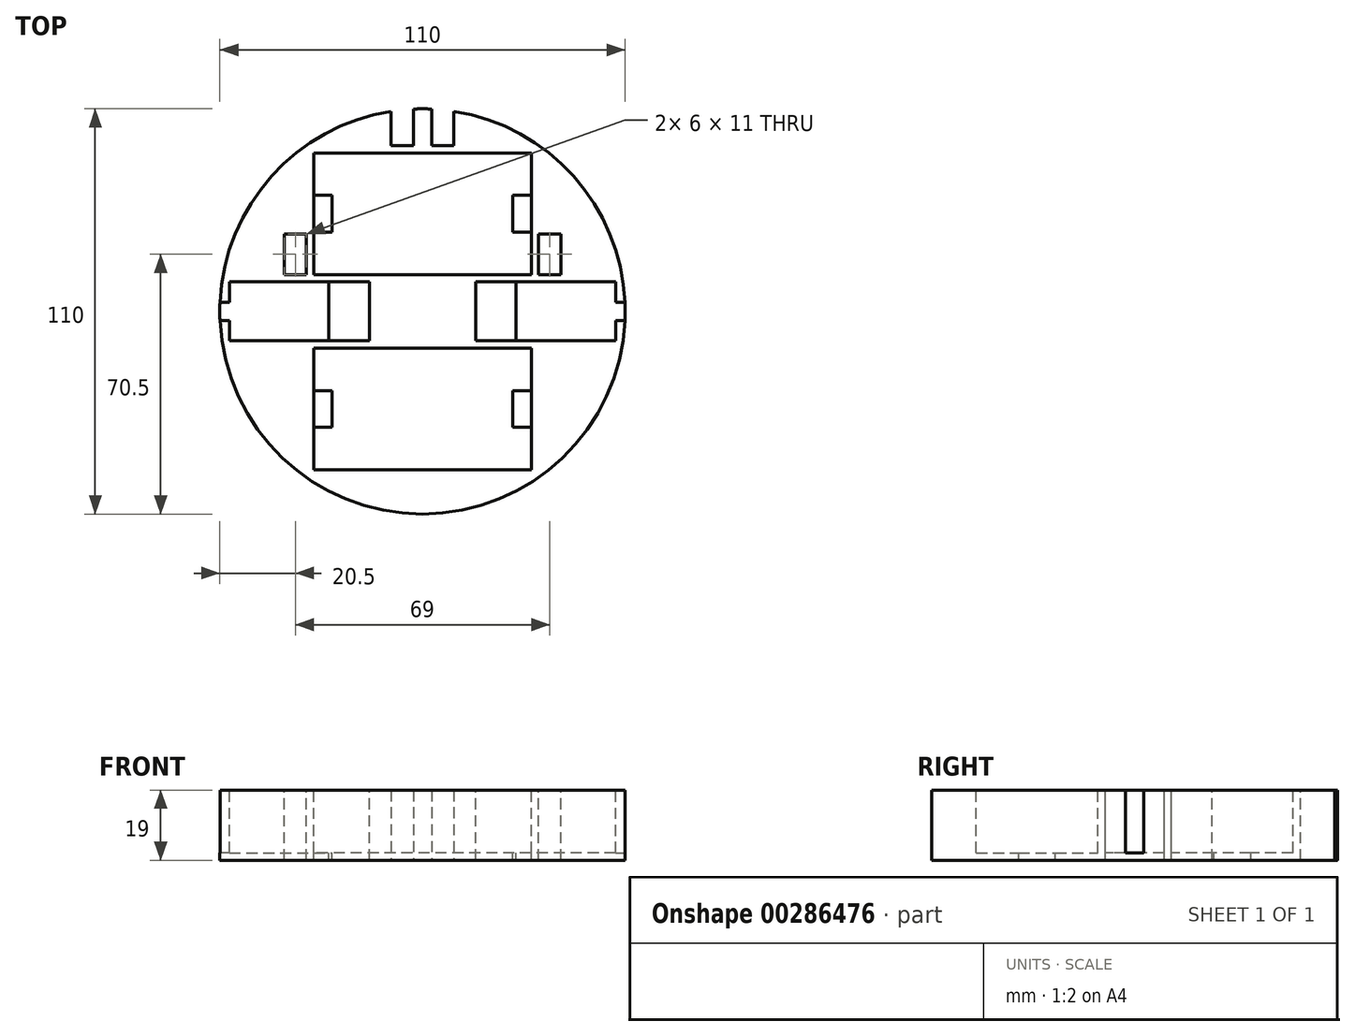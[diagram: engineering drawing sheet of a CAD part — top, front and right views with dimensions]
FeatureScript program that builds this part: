
annotation { "Feature Type Name" : "Feature", "Feature Type Description" : "" }
export const myFeature = defineFeature(function(context is Context, id is Id, definition is map)
    precondition{}
    {
        {
            var Q0;
            Q0=qCreatedBy(makeId("Top.planeOp"),FACE);
            var sketch = newSketch(context, id + "F0", { "sketchPlane" : qUnion([Q0])});
            skCircle(sketch, "E0", {"center": v(0, 0) * mm, "radius": 55 * mm});
            skSolve(sketch);
        }
        {
            var Q0;
            Q0=qSketchRegion(id+"F0",true);
            extrude(context, id + "F1", {"entities" : qUnion([Q0]), "depth" : 19 * mm, "offsetDistance" : 25 * mm});
        }
        {
            var Q0;
            Q0=makeQuery(id+"F1.opExtrude","CAP_FACE",FACE,{"disambiguationData":[OSD([sQuery(id+"F0.wireOp",EDGE,"E0")])],"isStart":false});
            var sketch = newSketch(context, id + "F2", { "sketchPlane" : qUnion([Q0])});
            skLineSegment(sketch, "E1.bottom", {"start": v(52.4, 8) * mm, "end": v(14.4, 8) * mm});
            skLineSegment(sketch, "E1.top", {"start": v(52.4, -8) * mm, "end": v(14.4, -8) * mm});
            skLineSegment(sketch, "E1.left", {"start": v(52.4, 8) * mm, "end": v(52.4, -8) * mm});
            skLineSegment(sketch, "E1.right", {"start": v(14.4, 8) * mm, "end": v(14.4, -8) * mm});
            skPoint(sketch, "E1.middle", {"position": v(33.4, 0) * mm});
            skLineSegment(sketch, "E2.bottom", {"start": v(52.4, 2.5) * mm, "end": v(57.6, 2.5) * mm});
            skLineSegment(sketch, "E2.top", {"start": v(52.4, -2.5) * mm, "end": v(57.6, -2.5) * mm});
            skLineSegment(sketch, "E2.left", {"start": v(52.4, 2.5) * mm, "end": v(52.4, -2.5) * mm});
            skLineSegment(sketch, "E2.right", {"start": v(57.6, 2.5) * mm, "end": v(57.6, -2.5) * mm});
            skPoint(sketch, "E2.middle", {"position": v(55, 0) * mm});
            skLineSegment(sketch, "E3.bottom", {"start": v(29.5, 43) * mm, "end": v(-29.5, 43) * mm});
            skLineSegment(sketch, "E3.top", {"start": v(29.5, 10) * mm, "end": v(-29.5, 10) * mm});
            skLineSegment(sketch, "E3.left", {"start": v(29.5, 43) * mm, "end": v(29.5, 10) * mm});
            skLineSegment(sketch, "E3.right", {"start": v(-29.5, 43) * mm, "end": v(-29.5, 10) * mm});
            skPoint(sketch, "E3.middle", {"position": v(0, 26.5) * mm});
            skLineSegment(sketch, "E4.MirrorCS", {"start": v(29.5, -10) * mm, "end": v(-29.5, -10) * mm});
            skLineSegment(sketch, "E5.MirrorCS", {"start": v(29.5, -43) * mm, "end": v(29.5, -10) * mm});
            skLineSegment(sketch, "E6.MirrorCS", {"start": v(29.5, -43) * mm, "end": v(-29.5, -43) * mm});
            skLineSegment(sketch, "E7.MirrorCS", {"start": v(-29.5, -43) * mm, "end": v(-29.5, -10) * mm});
            skLineSegment(sketch, "E8.MirrorCS", {"start": v(-52.4, 8) * mm, "end": v(-14.4, 8) * mm});
            skLineSegment(sketch, "E9.MirrorCS", {"start": v(-14.4, 8) * mm, "end": v(-14.4, -8) * mm});
            skLineSegment(sketch, "E10.MirrorCS", {"start": v(-52.4, -8) * mm, "end": v(-14.4, -8) * mm});
            skLineSegment(sketch, "E11.MirrorCS", {"start": v(-52.4, -2.5) * mm, "end": v(-57.6, -2.5) * mm});
            skLineSegment(sketch, "E12.MirrorCS", {"start": v(-57.6, 2.5) * mm, "end": v(-57.6, -2.5) * mm});
            skLineSegment(sketch, "E13.MirrorCS", {"start": v(-52.4, 2.5) * mm, "end": v(-57.6, 2.5) * mm});
            skLineSegment(sketch, "E14.MirrorCS", {"start": v(-52.4, 8) * mm, "end": v(-52.4, -8) * mm});
            skSolve(sketch);
        }
        {
            var Q0;
            Q0=qSketchRegion(id+"F2",true);
            extrude(context, id + "F3", {"entities" : qUnion([Q0]), "operationType" : NewBodyOperationType.REMOVE, "oppositeDirection" : true, "depth" : 17 * mm, "offsetDistance" : 25 * mm});
        }
        {
            var Q0;
            Q0=makeQuery(id+"F1.opExtrude","CAP_FACE",FACE,{"disambiguationData":[OSD([sQuery(id+"F0.wireOp",EDGE,"E0")])],"isStart":false});
            var sketch = newSketch(context, id + "F4", { "sketchPlane" : qUnion([Q0])});
            skLineSegment(sketch, "E15.bottom", {"start": v(-37.5, 21) * mm, "end": v(-31.5, 21) * mm});
            skLineSegment(sketch, "E15.top", {"start": v(-37.5, 10) * mm, "end": v(-31.5, 10) * mm});
            skLineSegment(sketch, "E15.left", {"start": v(-37.5, 21) * mm, "end": v(-37.5, 10) * mm});
            skLineSegment(sketch, "E15.right", {"start": v(-31.5, 21) * mm, "end": v(-31.5, 10) * mm});
            skLineSegment(sketch, "E16.MirrorCS", {"start": v(37.5, 21) * mm, "end": v(37.5, 10) * mm});
            skLineSegment(sketch, "E17.MirrorCS", {"start": v(37.5, 10) * mm, "end": v(31.5, 10) * mm});
            skLineSegment(sketch, "E18.MirrorCS", {"start": v(37.5, 21) * mm, "end": v(31.5, 21) * mm});
            skLineSegment(sketch, "E19.MirrorCS", {"start": v(31.5, 21) * mm, "end": v(31.5, 10) * mm});
            skLineSegment(sketch, "E20.bottom", {"start": v(-8.5, 56) * mm, "end": v(-2.5, 56) * mm});
            skLineSegment(sketch, "E20.top", {"start": v(-8.5, 45) * mm, "end": v(-2.5, 45) * mm});
            skLineSegment(sketch, "E20.left", {"start": v(-8.5, 56) * mm, "end": v(-8.5, 45) * mm});
            skLineSegment(sketch, "E20.right", {"start": v(-2.5, 56) * mm, "end": v(-2.5, 45) * mm});
            skLineSegment(sketch, "E21.MirrorCS", {"start": v(8.5, 56) * mm, "end": v(2.5, 56) * mm});
            skLineSegment(sketch, "E22.MirrorCS", {"start": v(8.5, 56) * mm, "end": v(8.5, 45) * mm});
            skLineSegment(sketch, "E23.MirrorCS", {"start": v(2.5, 56) * mm, "end": v(2.5, 45) * mm});
            skLineSegment(sketch, "E24.MirrorCS", {"start": v(8.5, 45) * mm, "end": v(2.5, 45) * mm});
            skLineSegment(sketch, "E25.bottom", {"start": v(-14.4, 8) * mm, "end": v(-25.4, 8) * mm});
            skLineSegment(sketch, "E25.top", {"start": v(-14.4, -8) * mm, "end": v(-25.4, -8) * mm});
            skLineSegment(sketch, "E25.left", {"start": v(-14.4, 8) * mm, "end": v(-14.4, -8) * mm});
            skLineSegment(sketch, "E25.right", {"start": v(-25.4, 8) * mm, "end": v(-25.4, -8) * mm});
            skLineSegment(sketch, "E26.MirrorCS", {"start": v(14.4, 8) * mm, "end": v(14.4, -8) * mm});
            skLineSegment(sketch, "E27.MirrorCS", {"start": v(14.4, -8) * mm, "end": v(25.4, -8) * mm});
            skLineSegment(sketch, "E28.MirrorCS", {"start": v(14.4, 8) * mm, "end": v(25.4, 8) * mm});
            skLineSegment(sketch, "E29.MirrorCS", {"start": v(25.4, 8) * mm, "end": v(25.4, -8) * mm});
            skLineSegment(sketch, "E30.bottom", {"start": v(29.5, 31.5) * mm, "end": v(24.5, 31.5) * mm});
            skLineSegment(sketch, "E30.top", {"start": v(29.5, 21.5) * mm, "end": v(24.5, 21.5) * mm});
            skLineSegment(sketch, "E30.left", {"start": v(29.5, 31.5) * mm, "end": v(29.5, 21.5) * mm});
            skLineSegment(sketch, "E30.right", {"start": v(24.5, 31.5) * mm, "end": v(24.5, 21.5) * mm});
            skPoint(sketch, "E30.middle", {"position": v(27, 26.5) * mm});
            skPoint(sketch, "E30.middle.positionSnap0", {"position": v(29.5, 26.5) * mm});
            skPoint(sketch, "E30.centerSnap0", {"position": v(29.5, 26.5) * mm});
            skPoint(sketch, "E31.MirrorP", {"position": v(-29.5, 26.5) * mm});
            skPoint(sketch, "E32.MirrorP", {"position": v(-27, 26.5) * mm});
            skLineSegment(sketch, "E33.MirrorCS", {"start": v(-29.5, 31.5) * mm, "end": v(-24.5, 31.5) * mm});
            skLineSegment(sketch, "E34.MirrorCS", {"start": v(-24.5, 31.5) * mm, "end": v(-24.5, 21.5) * mm});
            skLineSegment(sketch, "E35.MirrorCS", {"start": v(-29.5, 31.5) * mm, "end": v(-29.5, 21.5) * mm});
            skLineSegment(sketch, "E36.MirrorCS", {"start": v(-29.5, 21.5) * mm, "end": v(-24.5, 21.5) * mm});
            skPoint(sketch, "E37.MirrorP", {"position": v(29.5, -26.5) * mm});
            skPoint(sketch, "E38.MirrorP", {"position": v(-29.5, -26.5) * mm});
            skLineSegment(sketch, "E39.MirrorCS", {"start": v(29.5, -21.5) * mm, "end": v(24.5, -21.5) * mm});
            skLineSegment(sketch, "E40.MirrorCS", {"start": v(29.5, -31.5) * mm, "end": v(24.5, -31.5) * mm});
            skPoint(sketch, "E41.MirrorP", {"position": v(-27, -26.5) * mm});
            skLineSegment(sketch, "E42.MirrorCS", {"start": v(29.5, -31.5) * mm, "end": v(29.5, -21.5) * mm});
            skLineSegment(sketch, "E43.MirrorCS", {"start": v(-24.5, -31.5) * mm, "end": v(-24.5, -21.5) * mm});
            skLineSegment(sketch, "E44.MirrorCS", {"start": v(-29.5, -31.5) * mm, "end": v(-24.5, -31.5) * mm});
            skLineSegment(sketch, "E45.MirrorCS", {"start": v(-29.5, -31.5) * mm, "end": v(-29.5, -21.5) * mm});
            skLineSegment(sketch, "E46.MirrorCS", {"start": v(24.5, -31.5) * mm, "end": v(24.5, -21.5) * mm});
            skPoint(sketch, "E47.MirrorP", {"position": v(27, -26.5) * mm});
            skLineSegment(sketch, "E48.MirrorCS", {"start": v(-29.5, -21.5) * mm, "end": v(-24.5, -21.5) * mm});
            skSolve(sketch);
        }
        {
            var Q0;
            Q0=qSketchRegion(id+"F4",true);
            extrude(context, id + "F5", {"entities" : qUnion([Q0]), "operationType" : NewBodyOperationType.REMOVE, "endBound" : BoundingType.THROUGH_ALL, "oppositeDirection" : true, "depth" : 25 * mm, "offsetDistance" : 25 * mm});
        }
    });
